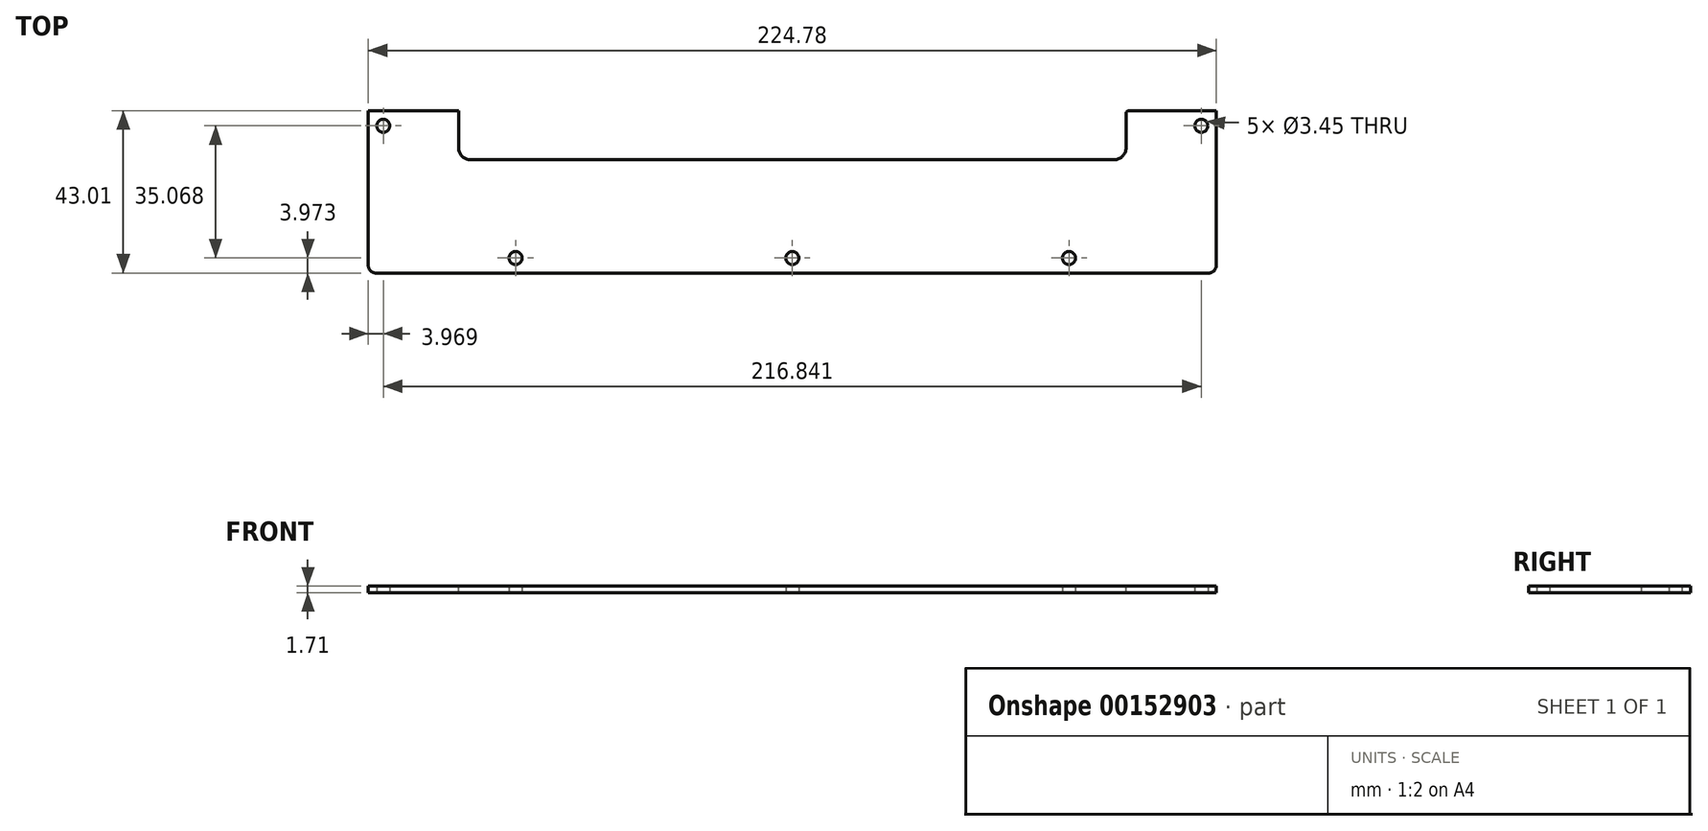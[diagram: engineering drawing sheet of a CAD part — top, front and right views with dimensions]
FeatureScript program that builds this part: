
annotation { "Feature Type Name" : "Feature", "Feature Type Description" : "" }
export const myFeature = defineFeature(function(context is Context, id is Id, definition is map)
    precondition{}
    {
        {
            var Q0;
            Q0=qCreatedBy(makeId("Top.planeOp"),FACE);
            var sketch = newSketch(context, id + "F0", { "sketchPlane" : qUnion([Q0])});
            skLineSegment(sketch, "E0.bottom", {"start": v(0, 0) * mm, "end": v(224.78, 0) * mm});
            skLineSegment(sketch, "E0.top", {"start": v(0, -43) * mm, "end": v(224.78, -43) * mm});
            skLineSegment(sketch, "E0.left", {"start": v(0, 0) * mm, "end": v(0, -43) * mm});
            skLineSegment(sketch, "E0.right", {"start": v(224.78, 0) * mm, "end": v(224.78, -43) * mm});
            skLineSegment(sketch, "E1", {"start": v(0, -3.97) * mm, "end": v(3.97, -3.97) * mm, "construction": true});
            skLineSegment(sketch, "E2", {"start": v(3.97, -3.97) * mm, "end": v(3.97, 0) * mm, "construction": true});
            skLineSegment(sketch, "E3", {"start": v(220.8, 0) * mm, "end": v(220.8, -3.97) * mm, "construction": true});
            skLineSegment(sketch, "E4", {"start": v(220.8, -3.97) * mm, "end": v(224.78, -3.97) * mm, "construction": true});
            skLineSegment(sketch, "E5", {"start": v(112.39, -43) * mm, "end": v(112.39, -39.04) * mm, "construction": true});
            skLineSegment(sketch, "E6", {"start": v(112.39, -39.04) * mm, "end": v(185.74, -39.04) * mm, "construction": true});
            skLineSegment(sketch, "E7", {"start": v(112.39, -39.04) * mm, "end": v(39.04, -39.04) * mm, "construction": true});
            skCircle(sketch, "E8", {"center": v(3.97, -3.97) * mm, "radius": 1.73 * mm});
            skCircle(sketch, "E9", {"center": v(39.04, -39.04) * mm, "radius": 1.73 * mm});
            skCircle(sketch, "E10", {"center": v(112.39, -39.04) * mm, "radius": 1.73 * mm});
            skCircle(sketch, "E11", {"center": v(185.74, -39.04) * mm, "radius": 1.73 * mm});
            skCircle(sketch, "E12", {"center": v(220.8, -3.97) * mm, "radius": 1.73 * mm});
            skLineSegment(sketch, "E13", {"start": v(185.74, -3.97) * mm, "end": v(185.74, -39.04) * mm, "construction": true});
            skLineSegment(sketch, "E14", {"start": v(185.74, -3.97) * mm, "end": v(220.8, -3.97) * mm, "construction": true});
            skLineSegment(sketch, "E15", {"start": v(220.8, -3.97) * mm, "end": v(220.8, -3.97) * mm});
            skSolve(sketch);
        }
        {
            var Q0;
            Q0=qSketchRegion(id+"F0",true);
            extrude(context, id + "F1", {"entities" : qUnion([Q0]), "depth" : 1.7 * mm});
        }
        {
            var Q0;
            Q0=makeQuery(id+"F1.opExtrude","SWEPT_EDGE",EDGE,{"disambiguationData":[OSD([sQuery(id+"F0.wireOp",EDGE,"E0.top"),sQuery(id+"F0.wireOp",EDGE,"E0.left")])]});
            var Q1;
            Q1=makeQuery(id+"F1.opExtrude","SWEPT_EDGE",EDGE,{"disambiguationData":[OSD([sQuery(id+"F0.wireOp",EDGE,"E0.top"),sQuery(id+"F0.wireOp",EDGE,"E0.right")])]});
            fillet(context, id + "F2", {"entities" : qUnion([Q0, Q1]), "radius" : 1.98 * mm, "tangentPropagation" : true, "allowEdgeOverflow" : false});
        }
        {
            var Q0;
            Q0=makeQuery(id+"F1.opExtrude","CAP_FACE",FACE,{"disambiguationData":[OSD([sQuery(id+"F0.wireOp",EDGE,"E0.bottom"),sQuery(id+"F0.wireOp",EDGE,"E0.top"),sQuery(id+"F0.wireOp",EDGE,"E0.left"),sQuery(id+"F0.wireOp",EDGE,"E0.right"),sQuery(id+"F0.wireOp",EDGE,"E8"),sQuery(id+"F0.wireOp",EDGE,"E9"),sQuery(id+"F0.wireOp",EDGE,"E10"),sQuery(id+"F0.wireOp",EDGE,"E11"),sQuery(id+"F0.wireOp",EDGE,"E12")])],"isStart":false});
            var sketch = newSketch(context, id + "F3", { "sketchPlane" : qUnion([Q0])});
            skLineSegment(sketch, "E16.bottom", {"start": v(23.94, 0) * mm, "end": v(200.84, 0) * mm});
            skLineSegment(sketch, "E16.top", {"start": v(23.94, -13) * mm, "end": v(200.84, -13) * mm});
            skLineSegment(sketch, "E16.left", {"start": v(23.94, 0) * mm, "end": v(23.94, -13) * mm});
            skLineSegment(sketch, "E16.right", {"start": v(200.84, 0) * mm, "end": v(200.84, -13) * mm});
            skPoint(sketch, "E17", {"position": v(112.39, 0) * mm});
            skSolve(sketch);
        }
        {
            var Q0;
            Q0 = qSketchRegion(id + "F3", true);
            var Q1;
            Q1=makeQuery(id+"F1.opExtrude","CAP_FACE",FACE,{"disambiguationData":[OSD([sQuery(id+"F0.wireOp",EDGE,"E0.bottom"),sQuery(id+"F0.wireOp",EDGE,"E0.top"),sQuery(id+"F0.wireOp",EDGE,"E0.left"),sQuery(id+"F0.wireOp",EDGE,"E0.right"),sQuery(id+"F0.wireOp",EDGE,"E8"),sQuery(id+"F0.wireOp",EDGE,"E9"),sQuery(id+"F0.wireOp",EDGE,"E10"),sQuery(id+"F0.wireOp",EDGE,"E11"),sQuery(id+"F0.wireOp",EDGE,"E12")])],"isStart":true});
            extrude(context, id + "F4", {"entities" : qUnion([Q0]), "operationType" : NewBodyOperationType.REMOVE, "endBound" : BoundingType.UP_TO_SURFACE, "oppositeDirection" : true, "endBoundEntityFace" : qUnion([Q1]), "depth" : 25.4 * mm});
        }
        {
            var Q0;
            Q0=makeQuery(id+"F4.boolean.opBoolean","COPY",EDGE,{"derivedFrom":makeQuery(id+"F4.opExtrude","SWEPT_EDGE",EDGE,{"disambiguationData":[OSD([sQuery(id+"F3.wireOp",EDGE,"E16.top"),sQuery(id+"F3.wireOp",EDGE,"E16.right")])]})});
            var Q1;
            Q1=makeQuery(id+"F4.boolean.opBoolean","COPY",EDGE,{"derivedFrom":makeQuery(id+"F4.opExtrude","SWEPT_EDGE",EDGE,{"disambiguationData":[OSD([sQuery(id+"F3.wireOp",EDGE,"E16.top"),sQuery(id+"F3.wireOp",EDGE,"E16.left")])]})});
            fillet(context, id + "F5", {"entities" : qUnion([Q0, Q1]), "radius" : 3.17 * mm, "tangentPropagation" : true, "allowEdgeOverflow" : false});
        }
        {
            var Q0;
            Q0=makeQuery(id+"F4.boolean.opBoolean","COPY",EDGE,{"derivedFrom":makeQuery(id+"F4.opExtrude","SWEPT_EDGE",EDGE,{"disambiguationData":[OSD([sQuery(id+"F0.wireOp",EDGE,"E0.bottom"),sQuery(id+"F3.wireOp",EDGE,"E16.bottom"),sQuery(id+"F3.wireOp",EDGE,"E16.left")])]})});
            var Q1;
            Q1=makeQuery(id+"F4.boolean.opBoolean","COPY",EDGE,{"derivedFrom":makeQuery(id+"F4.opExtrude","SWEPT_EDGE",EDGE,{"disambiguationData":[OSD([sQuery(id+"F0.wireOp",EDGE,"E0.bottom"),sQuery(id+"F3.wireOp",EDGE,"E16.bottom"),sQuery(id+"F3.wireOp",EDGE,"E16.right")])]})});
            fillet(context, id + "F6", {"entities" : qUnion([Q0, Q1]), "radius" : 0.76 * mm, "tangentPropagation" : true, "allowEdgeOverflow" : false});
        }
    });
